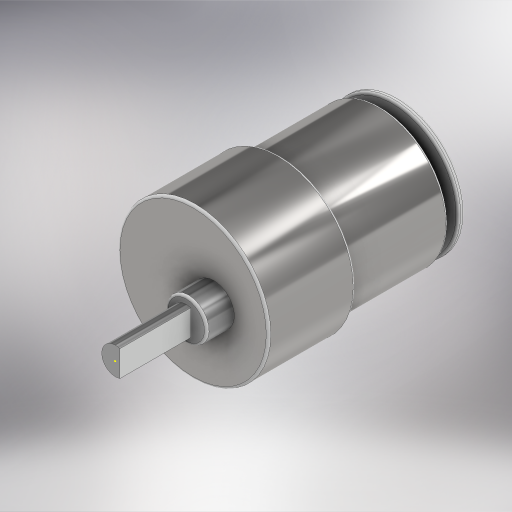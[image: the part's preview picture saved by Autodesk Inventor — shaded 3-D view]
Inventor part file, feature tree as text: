
AUTODESK INVENTOR PART (.ipt)
format: ipt  version: 2024 (Build 280153000, 153)  size: 439,296 bytes
history: native  units: mm
features: other x21, sketch x10, extrude x8, fillet x7
ambient origin geometry x8: Origin, YZ Plane, XZ Plane, XY Plane, X Axis, Y Axis, Z Axis, Center Point
bodies: Body1 (feature_tree)
feature tree (46):
  other  "Sólido1"
  extrude  "Extrusión1"  Depth=15.5mm TaperAngle=0.0deg
  extrude  "Extrusión2"  Depth=6.0mm TaperAngle=0.0deg
  sketch  "Boceto3"  dims[d6=1.0mm d7=15.5mm d8=0.0mm]
  sketch  "Boceto4"  dims[d9=4.5mm d10=33.0mm]
  extrude  "Extrusión3"  Depth=15.5mm TaperAngle=0.0deg
  extrude  "Extrusión4"  Depth=4.5mm
  extrude  "Extrusión5"  Depth=19.0mm
  extrude  "Extrusión6"  Depth=10.0mm
  extrude  "Extrusión7"  Depth=1.5mm TaperAngle=0.0deg
  extrude  "Extrusión8"  Depth=4.0mm TaperAngle=0.0deg
  fillet  "Empalme1"  Radius=0.5mm
  fillet  "Empalme2"  Radius=0.5mm
  fillet  "Empalme3"  Radius=0.5mm
  fillet  "Empalme4"  Radius=0.5mm
  fillet  "Empalme5"  Radius=0.5mm
  fillet  "Empalme6"  Radius=0.5mm
  fillet  "Empalme7"  Radius=1.0mm
  sketch  "Boceto1"  dims[d0=6.0mm d1=15.5mm d2=0.0mm]
  sketch  "Boceto2"  dims[d3=9.0mm d4=6.0mm d5=0.0mm]
  sketch  "Boceto5"  dims[d11=19.0mm d12=0.0mm d13=29.5mm]
  sketch  "Boceto6"  dims[d14=22.0mm d15=0.0mm d16=10.0mm]
  sketch  "Boceto7"  dims[d17=2.5mm d18=0.0mm d19=1.5mm d20=0.0mm]
  sketch  "Boceto8"  dims[d21=15.0mm d22=4.0mm d23=0.0mm d24=0.5mm d25=0.5mm d26=0.5mm d27=0.5mm d28=0.5mm d29=0.5mm d30=1.0mm]
  sketch  "Boceto9"
  sketch  "Boceto10"
  other  "Finish1"
  other  "Finish2"
  other  "Finish3"
  other  "Finish4"
  other  "Finish5"
  other  "Finish6"
  other  "Finish7"
  other  "Finish8"
  other  "Finish9"
  other  "Finish10"
  other  "Finish11"
  other  "Finish12"
  other  "Finish13"
  other  "Finish14"
  other  "Finish15"
  other  "Finish16"
  other  "Finish17"
  other  "Finish18"
  other  "Finish19"
  other  "Finish20"
